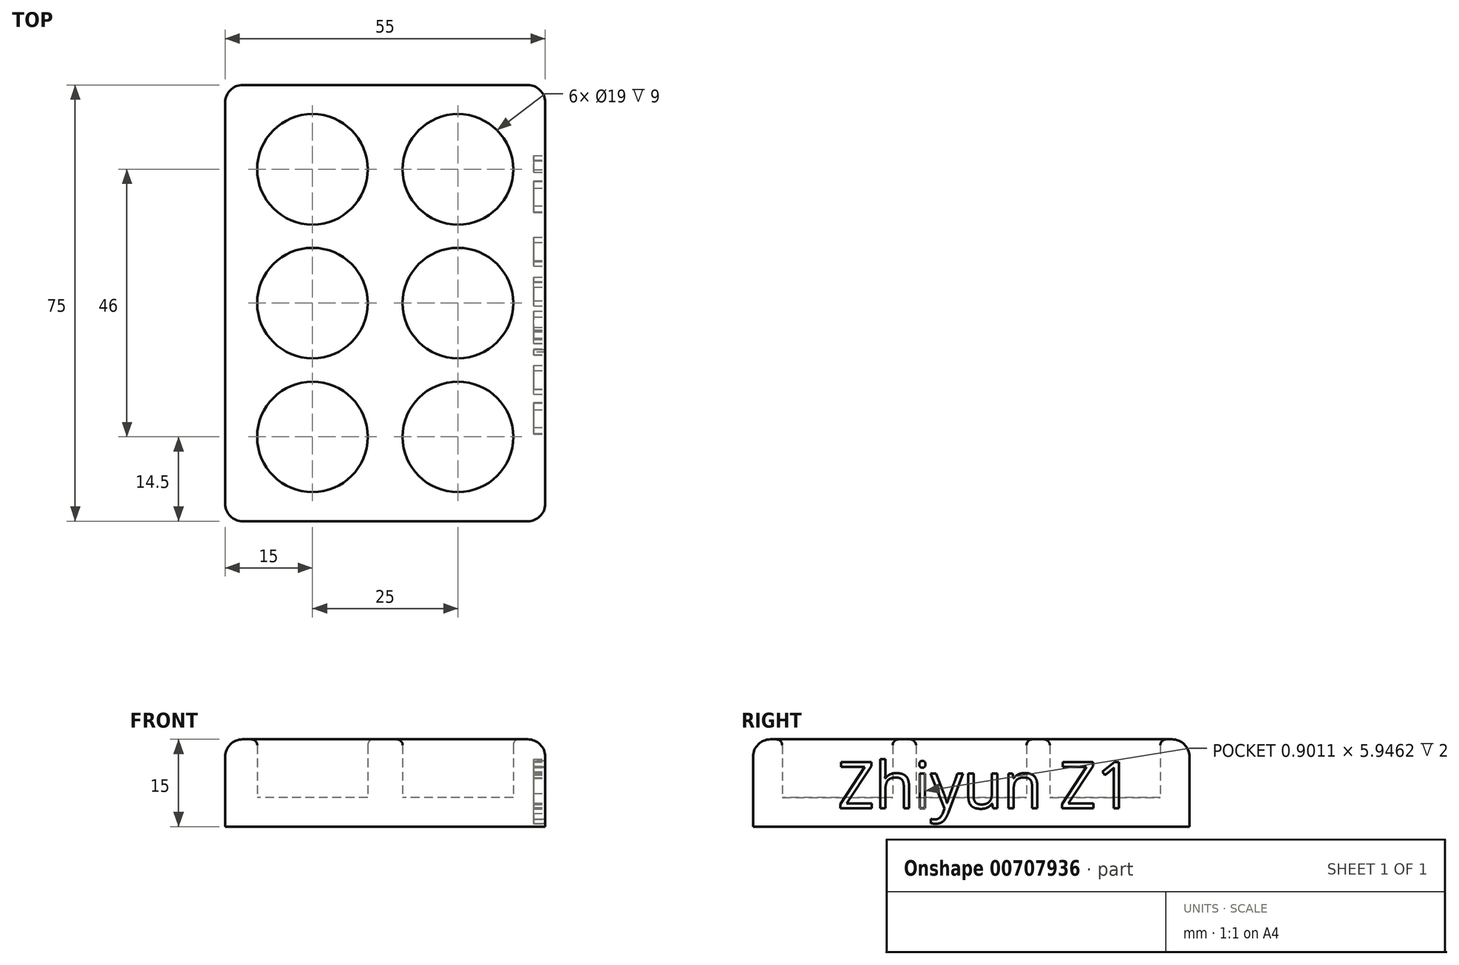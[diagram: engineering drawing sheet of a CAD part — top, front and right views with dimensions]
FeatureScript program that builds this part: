
annotation { "Feature Type Name" : "Feature", "Feature Type Description" : "" }
export const myFeature = defineFeature(function(context is Context, id is Id, definition is map)
    precondition{}
    {
        {
            var Q0;
            Q0=qCreatedBy(makeId("Top.planeOp"),FACE);
            var sketch = newSketch(context, id + "F0", { "sketchPlane" : qUnion([Q0])});
            skCircle(sketch, "E0", {"center": v(-12.5, -23) * mm, "radius": 9.5 * mm});
            skLineSegment(sketch, "E1.bottom", {"start": v(27.5, -37.5) * mm, "end": v(-27.5, -37.5) * mm});
            skLineSegment(sketch, "E1.top", {"start": v(27.5, 37.5) * mm, "end": v(-27.5, 37.5) * mm});
            skLineSegment(sketch, "E1.left", {"start": v(27.5, -37.5) * mm, "end": v(27.5, 37.5) * mm});
            skLineSegment(sketch, "E1.right", {"start": v(-27.5, -37.5) * mm, "end": v(-27.5, 37.5) * mm});
            skPoint(sketch, "E1.middle", {"position": v(0, 0) * mm});
            skCircle(sketch, "E2", {"center": v(12.5, -23) * mm, "radius": 9.5 * mm});
            skCircle(sketch, "E3", {"center": v(-12.5, 0) * mm, "radius": 9.5 * mm});
            skCircle(sketch, "E4", {"center": v(12.5, 0) * mm, "radius": 9.5 * mm});
            skCircle(sketch, "E5", {"center": v(-12.5, 23) * mm, "radius": 9.5 * mm});
            skCircle(sketch, "E6", {"center": v(12.5, 23) * mm, "radius": 9.5 * mm});
            skSolve(sketch);
        }
        {
            var Q0;
            Q0=makeQuery(id+"F0.imprint","IMPRINT",FACE,{"disambiguationData":[TD([[makeQuery(id+"F0.imprint","IMPRINT",EDGE,{"derivedFrom":sQuery(id+"F0.wireOp",EDGE,"E0")}),-1.0]])]});
            extrude(context, id + "F1", {"entities" : qUnion([Q0]), "depth" : 15 * mm, "offsetDistance" : 25 * mm});
        }
        {
            var Q0;
            Q0=makeQuery(id+"F0.imprint","IMPRINT",FACE,{"disambiguationData":[TD([[makeQuery(id+"F0.imprint","IMPRINT",EDGE,{"derivedFrom":sQuery(id+"F0.wireOp",EDGE,"E2")}),1.0]])]});
            var Q1;
            Q1=makeQuery(id+"F0.imprint","IMPRINT",FACE,{"disambiguationData":[TD([[makeQuery(id+"F0.imprint","IMPRINT",EDGE,{"derivedFrom":sQuery(id+"F0.wireOp",EDGE,"E4")}),1.0]])]});
            var Q2;
            Q2=makeQuery(id+"F0.imprint","IMPRINT",FACE,{"disambiguationData":[TD([[makeQuery(id+"F0.imprint","IMPRINT",EDGE,{"derivedFrom":sQuery(id+"F0.wireOp",EDGE,"E6")}),1.0]])]});
            var Q3;
            Q3=makeQuery(id+"F0.imprint","IMPRINT",FACE,{"disambiguationData":[TD([[makeQuery(id+"F0.imprint","IMPRINT",EDGE,{"derivedFrom":sQuery(id+"F0.wireOp",EDGE,"E5")}),1.0]])]});
            var Q4;
            Q4=makeQuery(id+"F0.imprint","IMPRINT",FACE,{"disambiguationData":[TD([[makeQuery(id+"F0.imprint","IMPRINT",EDGE,{"derivedFrom":sQuery(id+"F0.wireOp",EDGE,"E0")}),1.0]])]});
            var Q5;
            Q5=makeQuery(id+"F0.imprint","IMPRINT",FACE,{"disambiguationData":[TD([[makeQuery(id+"F0.imprint","IMPRINT",EDGE,{"derivedFrom":sQuery(id+"F0.wireOp",EDGE,"E3")}),1.0]])]});
            extrude(context, id + "F2", {"entities" : qUnion([Q0, Q1, Q2, Q3, Q4, Q5]), "operationType" : NewBodyOperationType.ADD, "depth" : 5 * mm, "offsetDistance" : 25 * mm});
        }
        {
            var Q0;
            Q0=makeQuery(id+"F1.opExtrude","SWEPT_EDGE",EDGE,{"disambiguationData":[OSD([sQuery(id+"F0.wireOp",EDGE,"E1.bottom"),sQuery(id+"F0.wireOp",EDGE,"E1.left")])]});
            var Q1;
            Q1=makeQuery(id+"F1.opExtrude","CAP_EDGE",EDGE,{"disambiguationData":[OSD([sQuery(id+"F0.wireOp",EDGE,"E1.left")])],"isStart":false});
            var Q2;
            Q2=makeQuery(id+"F1.opExtrude","CAP_EDGE",EDGE,{"disambiguationData":[OSD([sQuery(id+"F0.wireOp",EDGE,"E1.bottom")])],"isStart":false});
            var Q3;
            Q3=makeQuery(id+"F1.opExtrude","SWEPT_EDGE",EDGE,{"disambiguationData":[OSD([sQuery(id+"F0.wireOp",EDGE,"E1.bottom"),sQuery(id+"F0.wireOp",EDGE,"E1.right")])]});
            var Q4;
            Q4=makeQuery(id+"F1.opExtrude","CAP_EDGE",EDGE,{"disambiguationData":[OSD([sQuery(id+"F0.wireOp",EDGE,"E1.right")])],"isStart":false});
            var Q5;
            Q5=makeQuery(id+"F1.opExtrude","CAP_EDGE",EDGE,{"disambiguationData":[OSD([sQuery(id+"F0.wireOp",EDGE,"E1.top")])],"isStart":false});
            var Q6;
            Q6=makeQuery(id+"F1.opExtrude","SWEPT_EDGE",EDGE,{"disambiguationData":[OSD([sQuery(id+"F0.wireOp",EDGE,"E1.top"),sQuery(id+"F0.wireOp",EDGE,"E1.left")])]});
            var Q7;
            Q7=makeQuery(id+"F1.opExtrude","SWEPT_EDGE",EDGE,{"disambiguationData":[OSD([sQuery(id+"F0.wireOp",EDGE,"E1.top"),sQuery(id+"F0.wireOp",EDGE,"E1.right")])]});
            fillet(context, id + "F3", {"entities" : qUnion([Q0, Q1, Q2, Q3, Q4, Q5, Q6, Q7]), "radius" : 3 * mm, "tangentPropagation" : true, "allowEdgeOverflow" : false});
        }
        {
            var Q0;
            Q0=makeQuery(id+"F1.opExtrude","SWEPT_FACE",FACE,{"disambiguationData":[OSD([sQuery(id+"F0.wireOp",EDGE,"E1.left")])]});
            var sketch = newSketch(context, id + "F4", { "sketchPlane" : qUnion([Q0])});
            skText(sketch, "E7", { "text": "Zhiyun Z1", "fontName": "OpenSans-Regular.ttf"});
            const initialGuessF4  = {"E7": [-0.02297, 0.00315, 1, 0, 0.008]};
            skSetInitialGuess(sketch, initialGuessF4);
            skSolve(sketch);
        }
        {
            var Q0;
            Q0 = qSketchRegion(id + "F4", true);
            extrude(context, id + "F5", {"entities" : qUnion([Q0]), "operationType" : NewBodyOperationType.REMOVE, "oppositeDirection" : true, "depth" : 2 * mm, "offsetDistance" : 25 * mm});
        }
        {
            var Q0;
            Q0=makeQuery(id+"F1.opExtrude","CAP_EDGE",EDGE,{"disambiguationData":[OSD([sQuery(id+"F0.wireOp",EDGE,"E2")])],"isStart":false});
            var Q1;
            Q1=makeQuery(id+"F1.opExtrude","CAP_EDGE",EDGE,{"disambiguationData":[OSD([sQuery(id+"F0.wireOp",EDGE,"E0")])],"isStart":false});
            var Q2;
            Q2=makeQuery(id+"F1.opExtrude","CAP_EDGE",EDGE,{"disambiguationData":[OSD([sQuery(id+"F0.wireOp",EDGE,"E3")])],"isStart":false});
            var Q3;
            Q3=makeQuery(id+"F1.opExtrude","CAP_EDGE",EDGE,{"disambiguationData":[OSD([sQuery(id+"F0.wireOp",EDGE,"E4")])],"isStart":false});
            var Q4;
            Q4=makeQuery(id+"F1.opExtrude","CAP_EDGE",EDGE,{"disambiguationData":[OSD([sQuery(id+"F0.wireOp",EDGE,"E5")])],"isStart":false});
            var Q5;
            Q5=makeQuery(id+"F1.opExtrude","CAP_EDGE",EDGE,{"disambiguationData":[OSD([sQuery(id+"F0.wireOp",EDGE,"E6")])],"isStart":false});
            fillet(context, id + "F6", {"entities" : qUnion([Q0, Q1, Q2, Q3, Q4, Q5]), "radius" : 1 * mm, "tangentPropagation" : true, "allowEdgeOverflow" : false});
        }
    });
